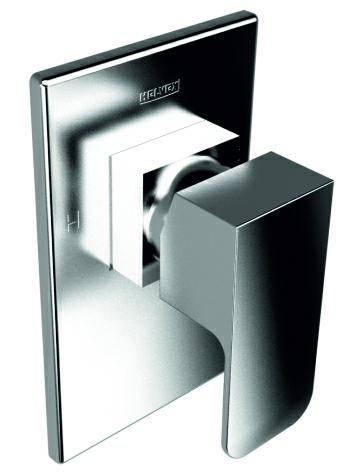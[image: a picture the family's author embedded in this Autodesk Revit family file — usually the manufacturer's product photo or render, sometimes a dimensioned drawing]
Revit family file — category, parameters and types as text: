
# Revit family: Monomando de Regadera E-792
name_source: partatom
category: Plumbing Fixtures
revit_build: Autodesk Revit 2015 (Build: 20140223_1515(x64)
units: mm (PartAtom-declared; Revit-internal decimal feet)

## types (1)
- E-793
    Brass Chromed = Brass
    Cartucho = Cartucho monomando cerámico con balanceo de presión Ø40mm
    Default Elevation = 1"
    Description = Monomando para Regadera con Balanceo de Presión sin Desviador.
    Garantía = El producto HELVEX está garantizado como libre de defectos en materiales y procesos de fabricación. El producto HELVEX está garantizado, en lo que se refiere a los acabados; por un periodo de 10 años en los acabados cromo y duravex, y por 2 años en cabados diferentes al cromo, a partir de la fecha de compra indicada en la factura.
    Instalación = ½" - 14 NPT
    Manufacturer = HELVEX S.A. DE C.V.
    Model = E-792
    Operación = Para abrir el flujo de agua levante la palanca maneral y gire para regular la temperatura.
    Presión máxima de trabajo = 85.3 psi
    Presión mínima de trabajo = 14.2 psi
    Satin = Satín
    Support Base Diameter = 5"
    Total Height = 6"
    Type Comments = Monomando Squadra
    Type Image = E-792.jpg
    URL = http://www.helvex.com.mx

## geometry (parser evidence)
native form markers: Sweep x3
no freeform markers — native parametric forms only
